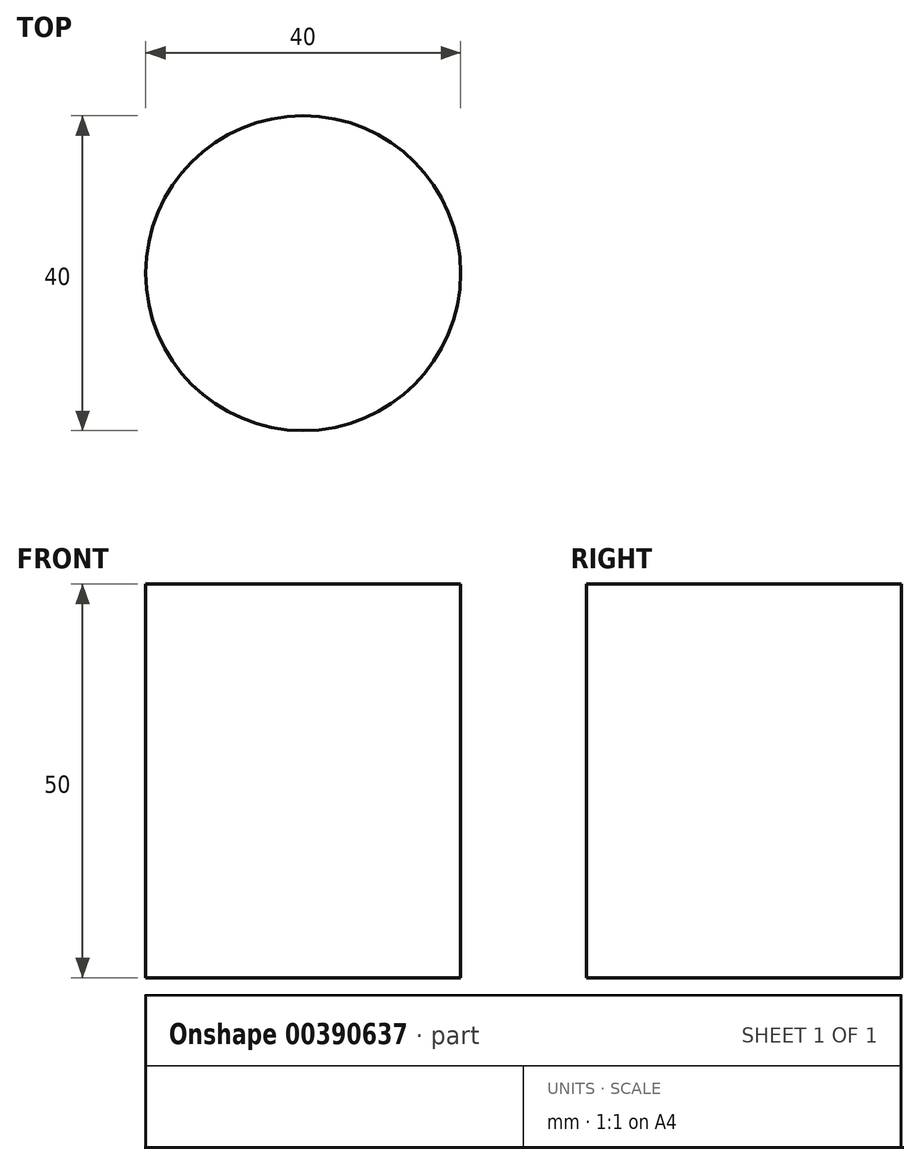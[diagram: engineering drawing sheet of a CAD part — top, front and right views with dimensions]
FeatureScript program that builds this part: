
annotation { "Feature Type Name" : "Feature", "Feature Type Description" : "" }
export const myFeature = defineFeature(function(context is Context, id is Id, definition is map)
    precondition{}
    {
        {
            var Q0;
            Q0=qCreatedBy(makeId("Top.planeOp"),FACE);
            var sketch = newSketch(context, id + "F0", { "sketchPlane" : qUnion([Q0])});
            skCircle(sketch, "E0", {"center": v(0, 0) * mm, "radius": 20 * mm});
            skSolve(sketch);
        }
        {
            var Q0;
            Q0=makeQuery(id+"F0.imprint","IMPRINT",FACE,{"disambiguationData":[TD([[makeQuery(id+"F0.imprint","IMPRINT",EDGE,{"derivedFrom":sQuery(id+"F0.wireOp",EDGE,"E0")}),1.0]])]});
            extrude(context, id + "F1", {"entities" : qUnion([Q0]), "depth" : 50 * mm});
        }
    });
